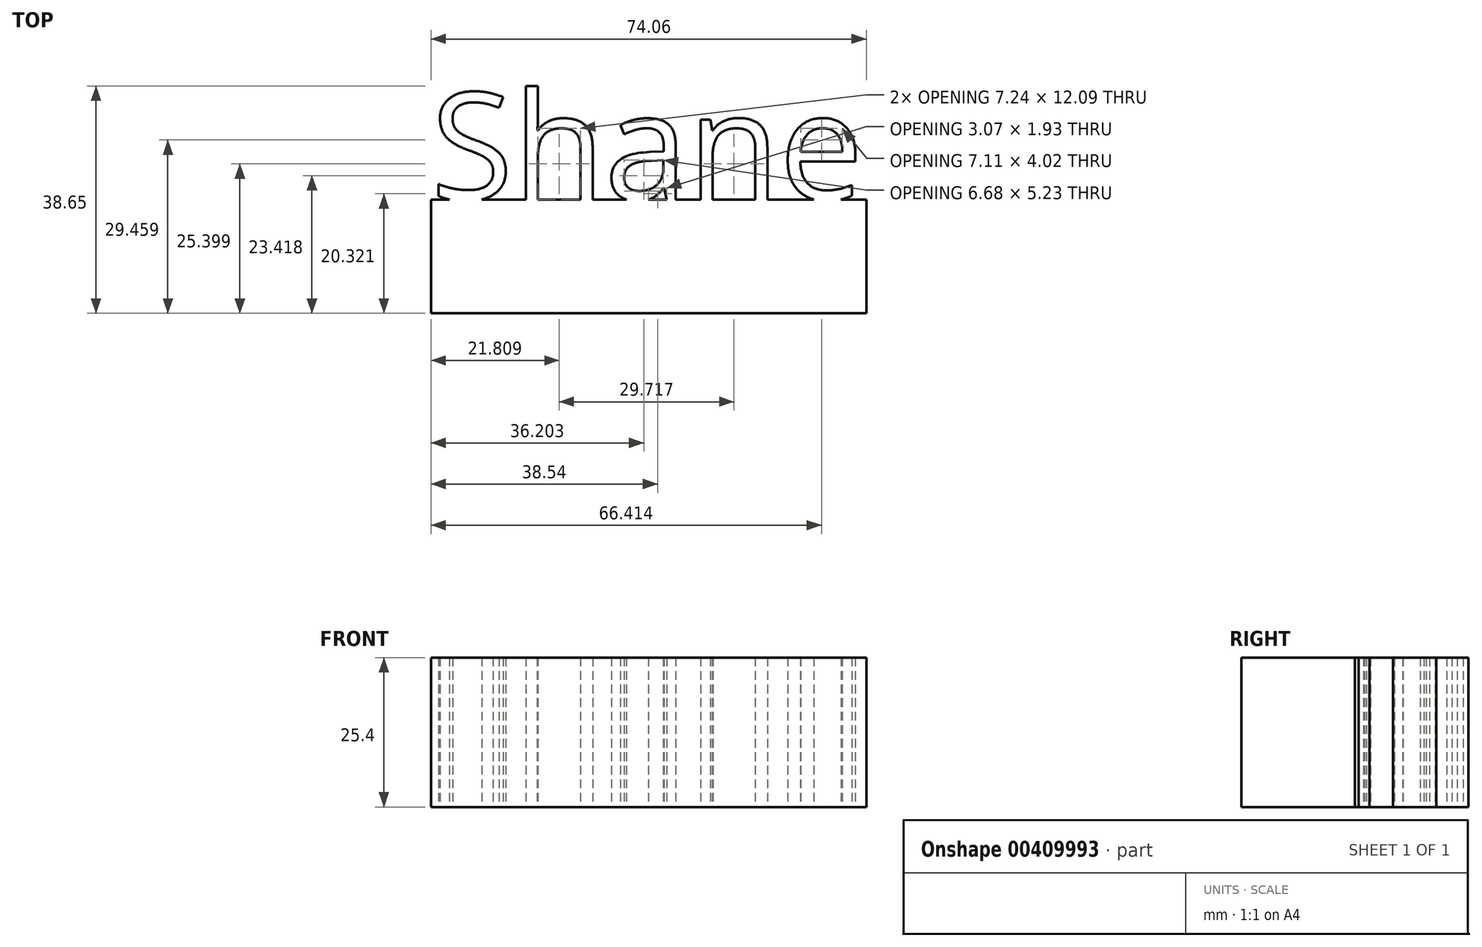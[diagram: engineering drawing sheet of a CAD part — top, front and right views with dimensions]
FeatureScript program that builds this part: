
annotation { "Feature Type Name" : "Feature", "Feature Type Description" : "" }
export const myFeature = defineFeature(function(context is Context, id is Id, definition is map)
    precondition{}
    {
        {
            var Q0;
            Q0=qCreatedBy(makeId("Top.planeOp"),FACE);
            var sketch = newSketch(context, id + "F0", { "sketchPlane" : qUnion([Q0])});
            skText(sketch, "E0", { "text": "Shane", "fontName": "OpenSans-Regular.ttf"});
            skLineSegment(sketch, "E1.bottom", {"start": v(-42.67, 19.35) * mm, "end": v(31.4, 19.35) * mm});
            skLineSegment(sketch, "E1.top", {"start": v(-42.67, 0) * mm, "end": v(31.4, 0) * mm});
            skLineSegment(sketch, "E1.left", {"start": v(-42.67, 19.35) * mm, "end": v(-42.67, 0) * mm});
            skLineSegment(sketch, "E1.right", {"start": v(31.4, 19.35) * mm, "end": v(31.4, 0) * mm});
            const initialGuessF0  = {"E0": [-0.04267, 0.01935, 1, 0, 0.01829]};
            skSetInitialGuess(sketch, initialGuessF0);
            skSolve(sketch);
        }
        {
            var Q0;
            Q0 = qSketchRegion(id + "F0", true);
            extrude(context, id + "F1", {"entities" : qUnion([Q0]), "depth" : 25.4 * mm});
        }
    });
